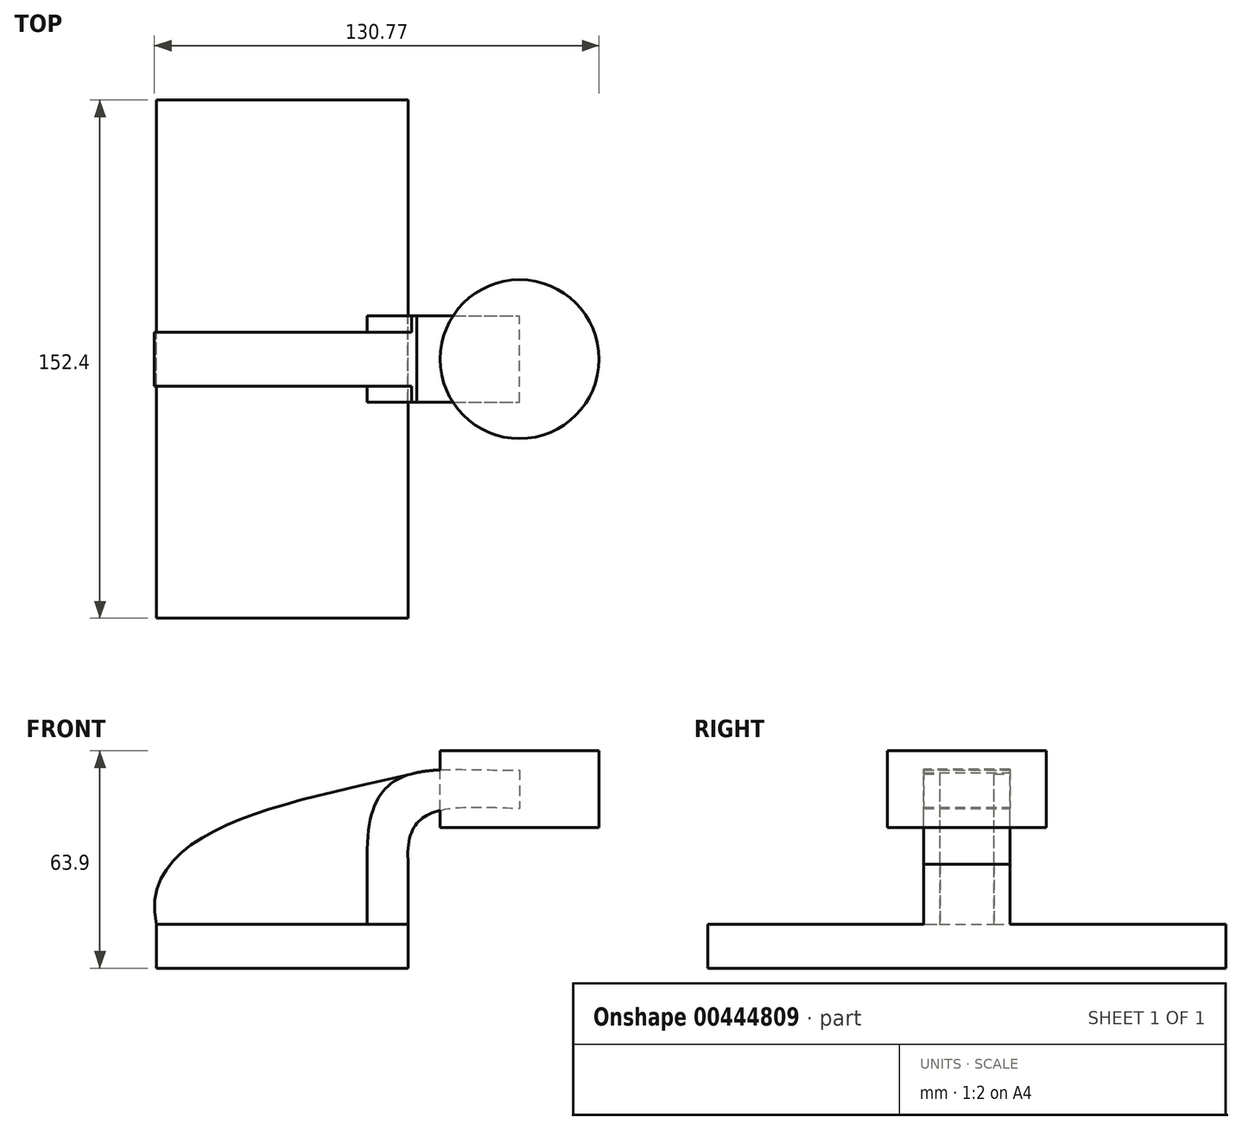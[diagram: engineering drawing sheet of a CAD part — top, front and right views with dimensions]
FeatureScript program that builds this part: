
annotation { "Feature Type Name" : "Feature", "Feature Type Description" : "" }
export const myFeature = defineFeature(function(context is Context, id is Id, definition is map)
    precondition{}
    {
        {
            var Q0;
            Q0=qCreatedBy(makeId("Front.planeOp"),FACE);
            var sketch = newSketch(context, id + "F0", { "sketchPlane" : qUnion([Q0])});
            skLineSegment(sketch, "E0.bottom", {"start": v(-4.56, -26.85) * mm, "end": v(-78.67, -26.85) * mm});
            skLineSegment(sketch, "E0.top", {"start": v(-4.56, -13.96) * mm, "end": v(-78.67, -13.96) * mm});
            skLineSegment(sketch, "E0.left", {"start": v(-4.56, -26.85) * mm, "end": v(-4.56, -13.96) * mm});
            skLineSegment(sketch, "E0.right", {"start": v(-78.67, -26.85) * mm, "end": v(-78.67, -13.96) * mm});
            skPoint(sketch, "E0.middle", {"position": v(-41.62, -20.4) * mm});
            skLineSegment(sketch, "E1", {"start": v(-4.56, -13.96) * mm, "end": v(-4.56, 3.76) * mm});
            skLineSegment(sketch, "E2", {"start": v(-4.56, 3.76) * mm, "end": v(-16.65, 3.76) * mm});
            skLineSegment(sketch, "E3", {"start": v(-16.65, 3.76) * mm, "end": v(-16.65, -13.96) * mm});
            skFitSpline(sketch, "E4", {"points": [v(-4.56, 3.76) * mm, v(28.2, 20.14) * mm], "startDerivative": vector(-4.83, 55.58) * mm, "endDerivative": vector(62.02, -2.42) * mm});
            skFitSpline(sketch, "E5", {"points": [v(-16.65, 3.76) * mm, v(28.2, 31.41) * mm], "startDerivative": vector(-3.22, 98.27) * mm, "endDerivative": vector(84.57, 0.8) * mm});
            skLineSegment(sketch, "E6.bottom", {"start": v(51.55, 14.5) * mm, "end": v(4.83, 14.5) * mm});
            skLineSegment(sketch, "E6.top", {"start": v(51.55, 37.05) * mm, "end": v(4.83, 37.05) * mm});
            skLineSegment(sketch, "E6.left", {"start": v(51.55, 14.5) * mm, "end": v(51.55, 37.05) * mm});
            skLineSegment(sketch, "E6.right", {"start": v(4.83, 14.5) * mm, "end": v(4.83, 37.05) * mm});
            skPoint(sketch, "E6.middle", {"position": v(28.2, 25.78) * mm});
            skLineSegment(sketch, "E7", {"start": v(28.2, 37.05) * mm, "end": v(28.2, 14.5) * mm});
            skFitSpline(sketch, "E8", {"points": [v(-78.67, -13.96) * mm, v(0, 31.14) * mm], "startDerivative": vector(-19.33, 90.21) * mm, "endDerivative": vector(100.68, 24.97) * mm});
            skSolve(sketch);
        }
        {
            var Q0;
            {var subQ3=sQuery(id+"F0.wireOp",EDGE,"E3");Q0=makeQuery(id+"F0.imprint","IMPRINT",FACE,{"disambiguationData":[TD([[makeQuery(id+"F0.imprint","IMPRINT",EDGE,{"derivedFrom":subQ3}),-1.0]])]});}
            extrude(context, id + "F1", {"entities" : qUnion([Q0]), "endBound" : BoundingType.SYMMETRIC, "depth" : 15.88 * mm});
        }
        {
            var Q0;
            Q0=makeQuery(id+"F0.imprint","IMPRINT",FACE,{"disambiguationData":[TD([[makeQuery(id+"F0.imprint","IMPRINT",EDGE,{"derivedFrom":sQuery(id+"F0.wireOp",EDGE,"E0.bottom")}),-1.0]])]});
            extrude(context, id + "F2", {"entities" : qUnion([Q0]), "operationType" : NewBodyOperationType.ADD, "endBound" : BoundingType.SYMMETRIC, "depth" : 152.4 * mm});
        }
        {
            var Q0;
            {var subQ0=sQuery(id+"F0.wireOp",EDGE,"E1");Q0=makeQuery(id+"F0.imprint","IMPRINT",FACE,{"disambiguationData":[TD([[makeQuery(id+"F0.imprint","IMPRINT",EDGE,{"derivedFrom":subQ0}),1.0]])]});}
            var Q1;
            {var subQ5=sQuery(id+"F0.wireOp",EDGE,"E2");Q1=makeQuery(id+"F0.imprint","IMPRINT",FACE,{"disambiguationData":[TD([[makeQuery(id+"F0.imprint","IMPRINT",EDGE,{"derivedFrom":subQ5}),-1.0]])]});}
            var Q2;
            {var subQ0=sQuery(id+"F0.wireOp",EDGE,"E7");var subQ1=sQuery(id+"F0.wireOp",EDGE,"E4");var subQ2=makeQuery(id+"F0.imprint","INTERSECT",VERTEX,{"derivedFrom":[subQ1,subQ0]});Q2=makeQuery(id+"F0.imprint","IMPRINT",FACE,{"disambiguationData":[TD([[makeQuery(id+"F0.imprint","IMPRINT",EDGE,{"disambiguationData":[TD([[subQ2,1.0]])],"derivedFrom":subQ1}),1.0]])]});}
            extrude(context, id + "F3", {"entities" : qUnion([Q0, Q1, Q2]), "operationType" : NewBodyOperationType.ADD, "endBound" : BoundingType.SYMMETRIC, "depth" : 25.4 * mm});
        }
        {
            var Q0;
            {var subQ4=sQuery(id+"F0.wireOp",EDGE,"E6.left");Q0=makeQuery(id+"F0.imprint","IMPRINT",FACE,{"disambiguationData":[TD([[makeQuery(id+"F0.imprint","IMPRINT",EDGE,{"derivedFrom":subQ4}),1.0]])]});}
            var Q1;
            Q1=sQuery(id+"F0.wireOp",EDGE,"E7");
            revolve(context, id + "F4", {"entities" : qUnion([Q0]), "axis" : qUnion([Q1]), "revolveType" : RevolveType.FULL});
        }
    });
